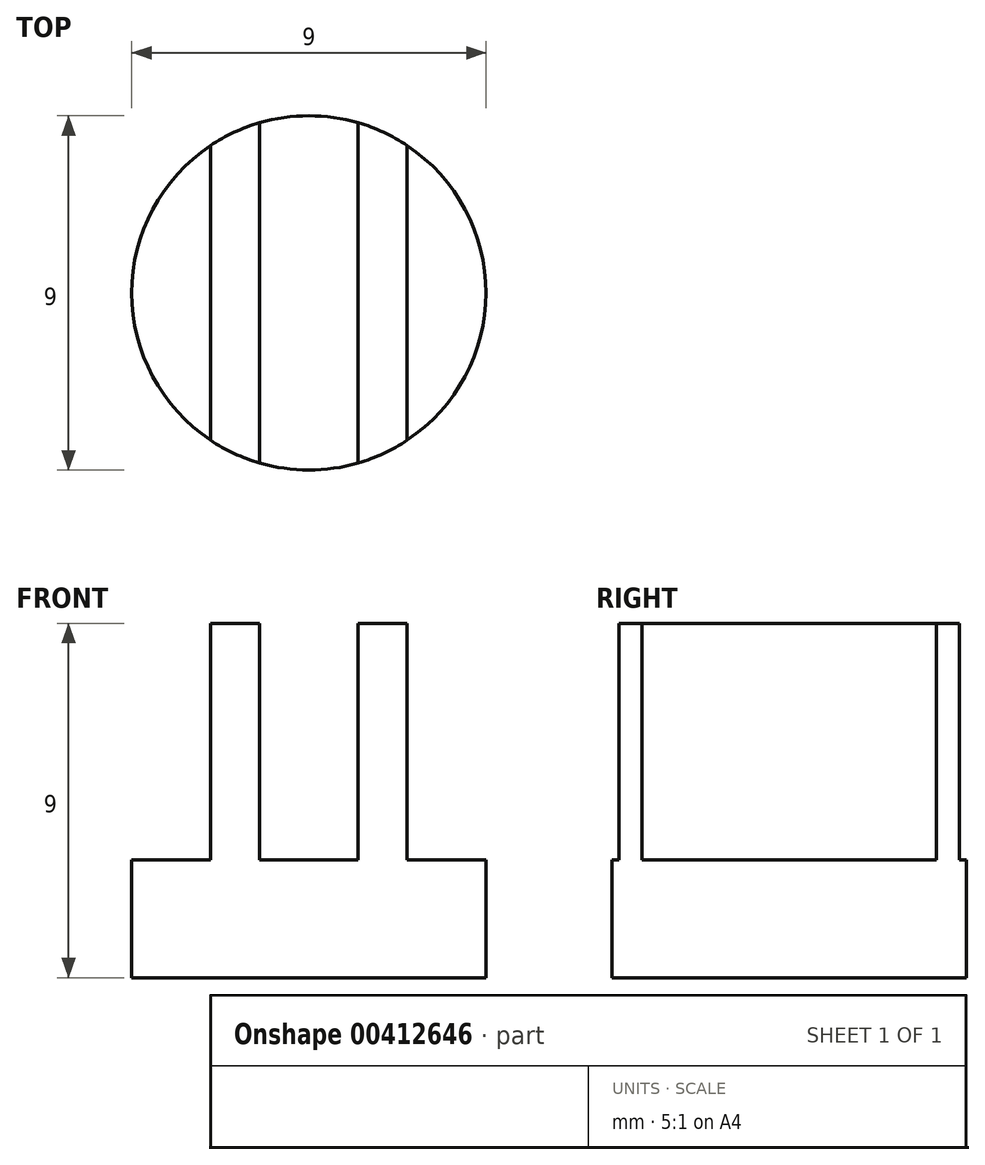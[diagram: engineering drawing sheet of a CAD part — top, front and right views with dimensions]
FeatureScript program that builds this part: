
annotation { "Feature Type Name" : "Feature", "Feature Type Description" : "" }
export const myFeature = defineFeature(function(context is Context, id is Id, definition is map)
    precondition{}
    {
        {
            var Q0;
            Q0=qCreatedBy(makeId("Top.planeOp"),FACE);
            var sketch = newSketch(context, id + "F0", { "sketchPlane" : qUnion([Q0])});
            skCircle(sketch, "E0", {"center": v(0, 0) * mm, "radius": 4.5 * mm});
            skLineSegment(sketch, "E1", {"start": v(1.25, 4.32) * mm, "end": v(1.25, -4.32) * mm});
            skLineSegment(sketch, "E2", {"start": v(2.5, 3.74) * mm, "end": v(2.5, -3.74) * mm});
            skLineSegment(sketch, "E3", {"start": v(-1.25, -4.32) * mm, "end": v(-1.25, 4.32) * mm});
            skLineSegment(sketch, "E4", {"start": v(-2.5, 3.74) * mm, "end": v(-2.5, -3.74) * mm});
            skSolve(sketch);
        }
        {
            var Q0;
            {var subQ0=sQuery(id+"F0.wireOp",EDGE,"E4");Q0=makeQuery(id+"F0.imprint","IMPRINT",FACE,{"disambiguationData":[TD([[makeQuery(id+"F0.imprint","IMPRINT",EDGE,{"derivedFrom":subQ0}),-1.0]])]});}
            var Q1;
            {var subQ0=sQuery(id+"F0.wireOp",EDGE,"E1");Q1=makeQuery(id+"F0.imprint","IMPRINT",FACE,{"disambiguationData":[TD([[makeQuery(id+"F0.imprint","IMPRINT",EDGE,{"derivedFrom":subQ0}),-1.0]])]});}
            var Q2;
            {var subQ0=sQuery(id+"F0.wireOp",EDGE,"E2");Q2=makeQuery(id+"F0.imprint","IMPRINT",FACE,{"disambiguationData":[TD([[makeQuery(id+"F0.imprint","IMPRINT",EDGE,{"derivedFrom":subQ0}),1.0]])]});}
            extrude(context, id + "F1", {"entities" : qUnion([Q0, Q1, Q2]), "depth" : 3 * mm, "offsetDistance" : 25 * mm});
        }
        {
            var Q0;
            {var subQ0=sQuery(id+"F0.wireOp",EDGE,"E3");Q0=makeQuery(id+"F0.imprint","IMPRINT",FACE,{"disambiguationData":[TD([[makeQuery(id+"F0.imprint","IMPRINT",EDGE,{"derivedFrom":subQ0}),1.0]])]});}
            var Q1;
            {var subQ0=sQuery(id+"F0.wireOp",EDGE,"E1");Q1=makeQuery(id+"F0.imprint","IMPRINT",FACE,{"disambiguationData":[TD([[makeQuery(id+"F0.imprint","IMPRINT",EDGE,{"derivedFrom":subQ0}),1.0]])]});}
            extrude(context, id + "F2", {"entities" : qUnion([Q0, Q1]), "operationType" : NewBodyOperationType.ADD, "depth" : 9 * mm, "offsetDistance" : 25 * mm});
        }
    });
